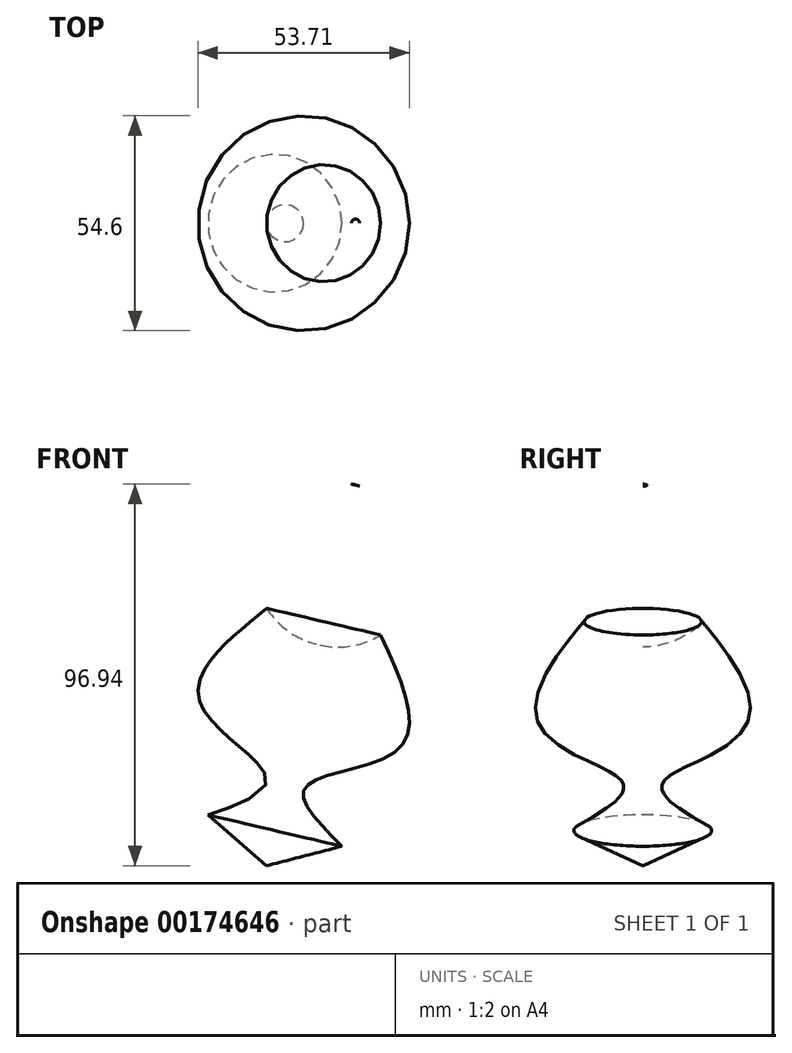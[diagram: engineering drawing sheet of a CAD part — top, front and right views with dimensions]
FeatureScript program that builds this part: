
annotation { "Feature Type Name" : "Feature", "Feature Type Description" : "" }
export const myFeature = defineFeature(function(context is Context, id is Id, definition is map)
    precondition{}
    {
        {
            var Q0;
            Q0=qCreatedBy(makeId("Front.planeOp"),FACE);
            var sketch = newSketch(context, id + "F0", { "sketchPlane" : qUnion([Q0])});
            skArc(sketch, "E0", {"start": v(-23.67, 40.9) * mm, "mid": v(17.08, 32.3) * mm, "end": v(-23.27, 42.64) * mm});
            skFitSpline(sketch, "E1", {"points": [v(-46.27, 9.53) * mm, v(-63.29, -14.22) * mm, v(-46.27, -33.58) * mm, v(-61.23, -42.97) * mm], "startDerivative": vector(-80.23, -65.14) * mm, "endDerivative": vector(-82.48, -27.67) * mm});
            skFitSpline(sketch, "E2", {"points": [v(-61.23, -42.97) * mm, v(-46.27, -55.87) * mm], "startDerivative": vector(14.96, -12.9) * mm, "endDerivative": vector(14.96, -12.9) * mm});
            skLineSegment(sketch, "E3", {"start": v(-23.67, 40.9) * mm, "end": v(-46.27, -55.87) * mm});
            skArc(sketch, "E4", {"start": v(-22.66, 40.6) * mm, "mid": v(-45.24, 33.26) * mm, "end": v(-46.27, 9.53) * mm});
            skLineSegment(sketch, "E5", {"start": v(-23.67, 40.9) * mm, "end": v(-22.66, 40.6) * mm});
            skSolve(sketch);
        }
        {
            var Q0;
            Q0 = qSketchRegion(id + "F0", true);
            var Q1;
            Q1=sQuery(id+"F0.wireOp",EDGE,"E3");
            revolve(context, id + "F1", {"entities" : qUnion([Q0]), "axis" : qUnion([Q1]), "revolveType" : RevolveType.FULL});
        }
    });
